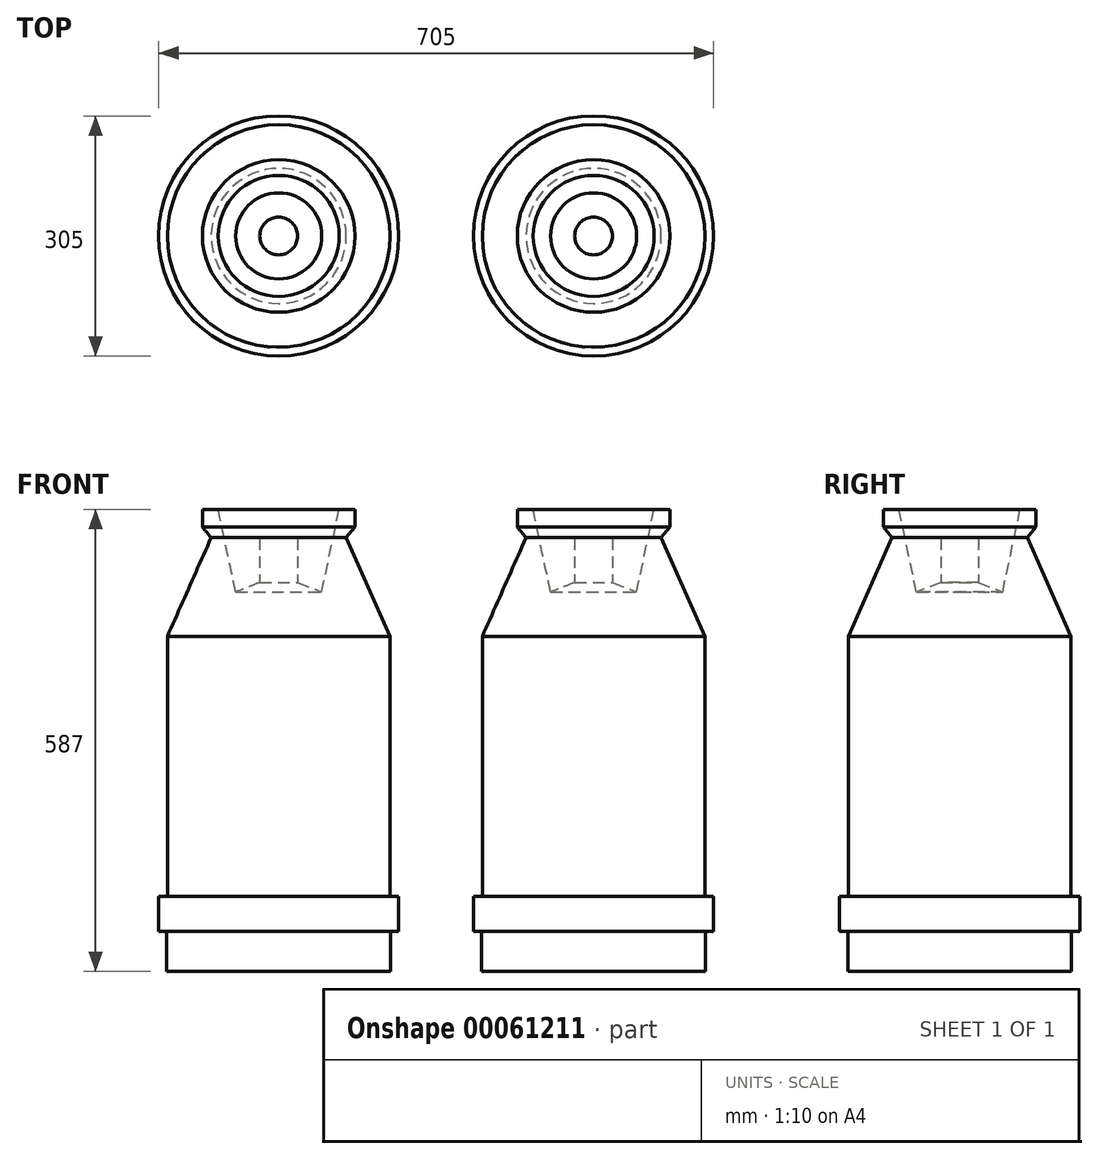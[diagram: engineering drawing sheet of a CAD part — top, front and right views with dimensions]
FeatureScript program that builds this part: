
annotation { "Feature Type Name" : "Feature", "Feature Type Description" : "" }
export const myFeature = defineFeature(function(context is Context, id is Id, definition is map)
    precondition{}
    {
        {
            var Q0;
            Q0=qCreatedBy(makeId("Front.planeOp"),FACE);
            var sketch = newSketch(context, id + "F0", { "sketchPlane" : qUnion([Q0])});
            skLineSegment(sketch, "E0", {"start": v(0, 0) * mm, "end": v(-142.19, 0) * mm});
            skLineSegment(sketch, "E1", {"start": v(-142.19, 0) * mm, "end": v(-142.19, 50.96) * mm});
            skLineSegment(sketch, "E2", {"start": v(-142.19, 50.96) * mm, "end": v(-152.5, 50.96) * mm});
            skLineSegment(sketch, "E3", {"start": v(-152.5, 50.96) * mm, "end": v(-152.5, 95.43) * mm});
            skLineSegment(sketch, "E4", {"start": v(-152.5, 95.43) * mm, "end": v(-141.38, 95.43) * mm});
            skLineSegment(sketch, "E5", {"start": v(-141.38, 95.43) * mm, "end": v(-141.38, 425.77) * mm});
            skLineSegment(sketch, "E6", {"start": v(-141.38, 425.77) * mm, "end": v(-85.8, 551.23) * mm});
            skLineSegment(sketch, "E7", {"start": v(-85.8, 551.23) * mm, "end": v(-96.91, 564.73) * mm});
            skLineSegment(sketch, "E8", {"start": v(-96.91, 564.73) * mm, "end": v(-96.91, 587) * mm});
            skLineSegment(sketch, "E9", {"start": v(-96.91, 587) * mm, "end": v(-76.88, 587) * mm});
            skLineSegment(sketch, "E10", {"start": v(-76.88, 587) * mm, "end": v(-54.69, 482.15) * mm});
            skLineSegment(sketch, "E11", {"start": v(-54.69, 482.15) * mm, "end": v(-24, 494.42) * mm});
            skLineSegment(sketch, "E12", {"start": v(-24, 494.42) * mm, "end": v(-24, 550.6) * mm});
            skLineSegment(sketch, "E13", {"start": v(-24, 550.6) * mm, "end": v(0, 550.6) * mm});
            skLineSegment(sketch, "E14", {"start": v(0, 550.6) * mm, "end": v(0, 0) * mm});
            skLineSegment(sketch, "E15", {"start": v(0, -69.47) * mm, "end": v(0, 742.5) * mm, "construction": true});
            skSolve(sketch);
        }
        {
            var Q0;
            Q0=makeQuery(id+"F0.imprint","IMPRINT",FACE,{"disambiguationData":[TD([[makeQuery(id+"F0.imprint","IMPRINT",EDGE,{"derivedFrom":sQuery(id+"F0.wireOp",EDGE,"E0")}),-1.0]])]});
            var Q1;
            Q1=sQuery(id+"F0.wireOp",EDGE,"E15");
            revolve(context, id + "F1", {"entities" : qUnion([Q0]), "axis" : qUnion([Q1]), "revolveType" : RevolveType.FULL});
        }
        {
            var Q0;
            Q0=makeQuery(id+"F1.opRevolve","SWEPT_BODY",BODY,{"disambiguationData":[OSD([sQuery(id+"F0.wireOp",EDGE,"E0"),sQuery(id+"F0.wireOp",EDGE,"E1"),sQuery(id+"F0.wireOp",EDGE,"E2"),sQuery(id+"F0.wireOp",EDGE,"E3"),sQuery(id+"F0.wireOp",EDGE,"E4"),sQuery(id+"F0.wireOp",EDGE,"E5"),sQuery(id+"F0.wireOp",EDGE,"E6"),sQuery(id+"F0.wireOp",EDGE,"E7"),sQuery(id+"F0.wireOp",EDGE,"E8"),sQuery(id+"F0.wireOp",EDGE,"E9"),sQuery(id+"F0.wireOp",EDGE,"E10"),sQuery(id+"F0.wireOp",EDGE,"E11"),sQuery(id+"F0.wireOp",EDGE,"E12"),sQuery(id+"F0.wireOp",EDGE,"E13"),sQuery(id+"F0.wireOp",EDGE,"E14")])]});
            var Q1;
            Q1=qCreatedBy(makeId("Right.planeOp"),FACE);
            transform(context, id + "F2", {"entities" : qUnion([Q0]), "transformType" : TransformType.TRANSLATION_DISTANCE, "transformDirection" : qUnion([Q1]), "distance" : 400 * mm, "makeCopy" : true});
        }
    });
